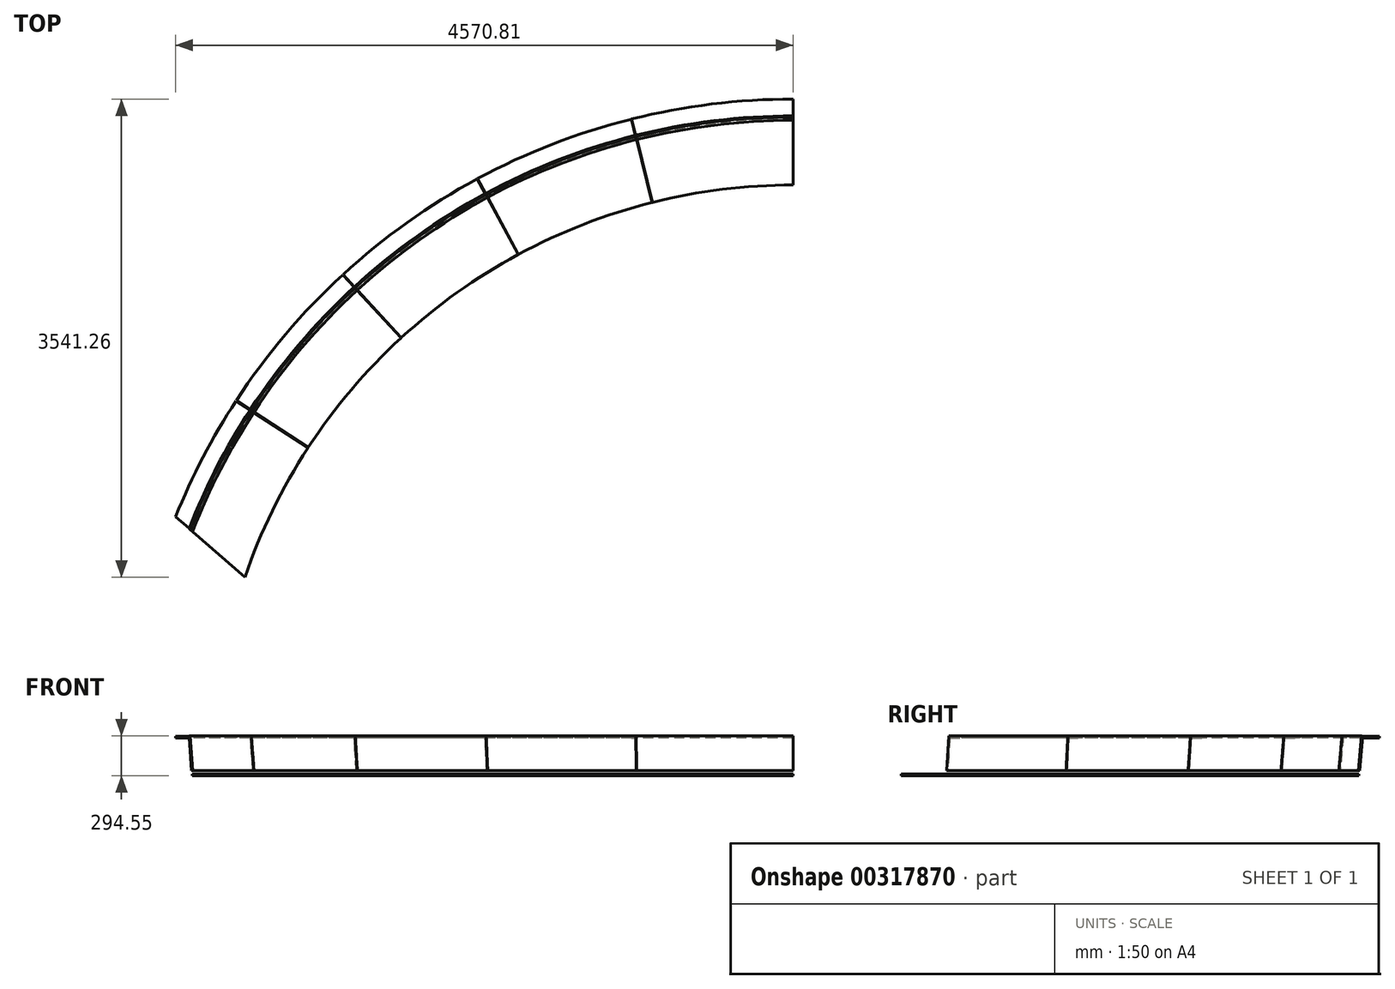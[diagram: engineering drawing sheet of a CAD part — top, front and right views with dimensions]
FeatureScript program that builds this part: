
annotation { "Feature Type Name" : "Feature", "Feature Type Description" : "" }
export const myFeature = defineFeature(function(context is Context, id is Id, definition is map)
    precondition{}
    {
        {
            var Q0;
            Q0=qCreatedBy(makeId("Top.planeOp"),FACE);
            var sketch = newSketch(context, id + "F0", { "sketchPlane" : qUnion([Q0])});
            skLineSegment(sketch, "E0", {"start": v(0, 0) * mm, "end": v(0, 473.08) * mm});
            skArc(sketch, "E1", {"start": v(0, 0) * mm, "mid": v(-2501.9, -802.3) * mm, "end": v(-4070.65, -2909.96) * mm});
            skLineSegment(sketch, "E2", {"start": v(-4070.65, -2909.96) * mm, "end": v(-4575.56, -2468.8) * mm});
            skLineSegment(sketch, "E3", {"start": v(0, 473.08) * mm, "end": v(0, 627.06) * mm});
            skArc(sketch, "E4", {"start": v(0, 627.06) * mm, "mid": v(-2762.25, -219.62) * mm, "end": v(-4575.56, -2468.8) * mm});
            skArc(sketch, "E5", {"start": v(0, 473.07) * mm, "mid": v(-2698.3, -362.37) * mm, "end": v(-4452.45, -2576.36) * mm});
            skArc(sketch, "E6", {"start": v(0, 498.48) * mm, "mid": v(-2708.85, -338.8) * mm, "end": v(-4472.79, -2558.6) * mm});
            skLineSegment(sketch, "E7", {"start": v(-1198.89, 479.04) * mm, "end": v(-1046.37, -129.2) * mm});
            skLineSegment(sketch, "E8", {"start": v(-2042.06, -515.53) * mm, "end": v(-2339.7, 36.39) * mm});
            skLineSegment(sketch, "E9", {"start": v(-2911.9, -1135.24) * mm, "end": v(-3336.32, -673.65) * mm});
            skLineSegment(sketch, "E10", {"start": v(-3602.27, -1950.12) * mm, "end": v(-4127.33, -1607.3) * mm});
            skSolve(sketch);
        }
        {
            var Q0;
            Q0=qCreatedBy(makeId("Top.planeOp"),FACE);
            var sketch = newSketch(context, id + "F1", { "sketchPlane" : qUnion([Q0])});
            skArc(sketch, "E11.0", {"start": v(-1.59, -12.7) * mm, "mid": v(-2497.27, -814.6) * mm, "end": v(-4060.3, -2919) * mm});
            skLineSegment(sketch, "E12.0", {"start": v(-4059.75, -2917.37) * mm, "end": v(-4449.3, -2577.01) * mm});
            skArc(sketch, "E13.0", {"start": v(-1.59, 469.9) * mm, "mid": v(-2696.94, -365.28) * mm, "end": v(-4449.3, -2577.01) * mm});
            skLineSegment(sketch, "E14.0", {"start": v(-1.59, -12.7) * mm, "end": v(-1.59, 469.9) * mm});
            skLineSegment(sketch, "E15.0", {"start": v(-1162.2, 326.21) * mm, "end": v(-1044.82, -141.9) * mm});
            skLineSegment(sketch, "E16.0", {"start": v(-1159.12, 326.98) * mm, "end": v(-1041.74, -141.12) * mm});
            skLineSegment(sketch, "E17.0", {"start": v(-2034.63, -525.96) * mm, "end": v(-2263.7, -101.19) * mm});
            skLineSegment(sketch, "E18.0", {"start": v(-2037.43, -527.47) * mm, "end": v(-2266.5, -102.7) * mm});
            skLineSegment(sketch, "E19.0", {"start": v(-2902.13, -1143.52) * mm, "end": v(-3228.78, -788.27) * mm});
            skLineSegment(sketch, "E20.0", {"start": v(-2904.47, -1145.67) * mm, "end": v(-3231.12, -790.41) * mm});
            skLineSegment(sketch, "E21.0", {"start": v(-3592.5, -1958.4) * mm, "end": v(-3996.6, -1694.56) * mm});
            skLineSegment(sketch, "E22.0", {"start": v(-3590.77, -1955.74) * mm, "end": v(-3994.86, -1691.9) * mm});
            skSolve(sketch);
        }
        {
            var Q0;
            {var subQ0=sQuery(id+"F1.wireOp",EDGE,"E12.0");Q0=makeQuery(id+"F1.imprint","IMPRINT",FACE,{"disambiguationData":[TD([[makeQuery(id+"F1.imprint","IMPRINT",EDGE,{"derivedFrom":subQ0}),-1.0]])]});}
            var Q1;
            {var subQ0=sQuery(id+"F1.wireOp",EDGE,"E20.0");Q1=makeQuery(id+"F1.imprint","IMPRINT",FACE,{"disambiguationData":[TD([[makeQuery(id+"F1.imprint","IMPRINT",EDGE,{"derivedFrom":subQ0}),1.0]])]});}
            var Q2;
            {var subQ0=sQuery(id+"F1.wireOp",EDGE,"E18.0");Q2=makeQuery(id+"F1.imprint","IMPRINT",FACE,{"disambiguationData":[TD([[makeQuery(id+"F1.imprint","IMPRINT",EDGE,{"derivedFrom":subQ0}),1.0]])]});}
            var Q3;
            {var subQ0=sQuery(id+"F1.wireOp",EDGE,"E15.0");Q3=makeQuery(id+"F1.imprint","IMPRINT",FACE,{"disambiguationData":[TD([[makeQuery(id+"F1.imprint","IMPRINT",EDGE,{"derivedFrom":subQ0}),-1.0]])]});}
            var Q4;
            {var subQ0=sQuery(id+"F1.wireOp",EDGE,"E14.0");Q4=makeQuery(id+"F1.imprint","IMPRINT",FACE,{"disambiguationData":[TD([[makeQuery(id+"F1.imprint","IMPRINT",EDGE,{"derivedFrom":subQ0}),1.0]])]});}
            extrude(context, id + "F2", {"entities" : qUnion([Q0, Q1, Q2, Q3, Q4]), "depth" : 12.7 * mm});
        }
        {
            var Q0;
            Q0=qCreatedBy(makeId("Top.planeOp"),FACE);
            cPlane(context, id + "F3", {"entities" : qUnion([Q0]), "cplaneType" : CPlaneType.OFFSET, "offset" : 281 * mm, "width" : 152.4 * mm, "height" : 152.4 * mm});
        }
        {
            var Q0;
            Q0=qCreatedBy(id+"F3.planeOp",FACE);
            var sketch = newSketch(context, id + "F4", { "sketchPlane" : qUnion([Q0])});
            skLineSegment(sketch, "E23.0", {"start": v(-1196.58, 476.35) * mm, "end": v(-1166.07, 354.7) * mm});
            skLineSegment(sketch, "E24.0", {"start": v(-1199.66, 475.58) * mm, "end": v(-1169.15, 353.93) * mm});
            skLineSegment(sketch, "E25.0", {"start": v(-2277.27, -76.04) * mm, "end": v(-2336.8, 34.35) * mm});
            skLineSegment(sketch, "E26.0", {"start": v(-2280.06, -77.55) * mm, "end": v(-2339.6, 32.84) * mm});
            skLineSegment(sketch, "E27.0", {"start": v(-3248.12, -767.23) * mm, "end": v(-3333, -674.91) * mm});
            skLineSegment(sketch, "E28.0", {"start": v(-3250.46, -769.38) * mm, "end": v(-3335.34, -677.06) * mm});
            skLineSegment(sketch, "E29.0", {"start": v(-4018.8, -1676.28) * mm, "end": v(-4123.8, -1607.71) * mm});
            skLineSegment(sketch, "E30.0", {"start": v(-4020.53, -1678.93) * mm, "end": v(-4125.54, -1610.37) * mm});
            skLineSegment(sketch, "E31.0", {"start": v(-4472.18, -2557.02) * mm, "end": v(-4572.4, -2469.44) * mm});
            skLineSegment(sketch, "E32.0", {"start": v(-1.59, 498.47) * mm, "end": v(-1.59, 623.89) * mm});
            skArc(sketch, "E33.0", {"start": v(-1.59, 623.89) * mm, "mid": v(-2761.13, -222.7) * mm, "end": v(-4572.62, -2469.97) * mm});
            skArc(sketch, "E34.0", {"start": v(-1.59, 498.47) * mm, "mid": v(-2708.8, -338.78) * mm, "end": v(-4472.18, -2557.02) * mm});
            skPoint(sketch, "E35.orphan", {"position": v(-4449.3, -2577.01) * mm});
            skPoint(sketch, "E36.orphan", {"position": v(-3996.6, -1694.56) * mm});
            skPoint(sketch, "E37.orphan", {"position": v(-3994.86, -1691.9) * mm});
            skPoint(sketch, "E38.orphan", {"position": v(-3231.12, -790.41) * mm});
            skPoint(sketch, "E39.orphan", {"position": v(-3228.78, -788.27) * mm});
            skPoint(sketch, "E40.orphan", {"position": v(-2263.7, -101.19) * mm});
            skPoint(sketch, "E41.orphan", {"position": v(-2266.5, -102.7) * mm});
            skPoint(sketch, "E42.orphan", {"position": v(-1159.12, 326.98) * mm});
            skPoint(sketch, "E43.orphan", {"position": v(-1162.2, 326.21) * mm});
            skPoint(sketch, "E44.orphan", {"position": v(-1.59, 469.9) * mm});
            skPoint(sketch, "E45.orphan", {"position": v(-4059.75, -2917.37) * mm});
            skPoint(sketch, "E46.orphan", {"position": v(-3590.77, -1955.74) * mm});
            skPoint(sketch, "E47.orphan", {"position": v(-2904.47, -1145.67) * mm});
            skPoint(sketch, "E48.orphan", {"position": v(-2037.43, -527.47) * mm});
            skPoint(sketch, "E49.orphan", {"position": v(-2902.13, -1143.52) * mm});
            skPoint(sketch, "E50.orphan", {"position": v(-3592.5, -1958.4) * mm});
            skPoint(sketch, "E51.orphan", {"position": v(-2034.63, -525.96) * mm});
            skPoint(sketch, "E52.orphan", {"position": v(-1041.74, -141.12) * mm});
            skPoint(sketch, "E53.orphan", {"position": v(-1044.82, -141.9) * mm});
            skPoint(sketch, "E54.orphan", {"position": v(-1.59, -12.7) * mm});
            skPoint(sketch, "E55.orphan", {"position": v(0, 498.48) * mm});
            skPoint(sketch, "E56.orphan", {"position": v(-4472.79, -2558.6) * mm});
            skSolve(sketch);
        }
        {
            var Q0;
            {var subQ0=sQuery(id+"F4.wireOp",EDGE,"E30.0");Q0=makeQuery(id+"F4.imprint","IMPRINT",FACE,{"disambiguationData":[TD([[makeQuery(id+"F4.imprint","IMPRINT",EDGE,{"derivedFrom":subQ0}),1.0]])]});}
            var Q1;
            {var subQ0=sQuery(id+"F4.wireOp",EDGE,"E28.0");Q1=makeQuery(id+"F4.imprint","IMPRINT",FACE,{"disambiguationData":[TD([[makeQuery(id+"F4.imprint","IMPRINT",EDGE,{"derivedFrom":subQ0}),1.0]])]});}
            var Q2;
            {var subQ0=sQuery(id+"F4.wireOp",EDGE,"E26.0");Q2=makeQuery(id+"F4.imprint","IMPRINT",FACE,{"disambiguationData":[TD([[makeQuery(id+"F4.imprint","IMPRINT",EDGE,{"derivedFrom":subQ0}),1.0]])]});}
            var Q3;
            {var subQ0=sQuery(id+"F4.wireOp",EDGE,"E24.0");Q3=makeQuery(id+"F4.imprint","IMPRINT",FACE,{"disambiguationData":[TD([[makeQuery(id+"F4.imprint","IMPRINT",EDGE,{"derivedFrom":subQ0}),-1.0]])]});}
            var Q4;
            {var subQ0=sQuery(id+"F4.wireOp",EDGE,"E23.0");Q4=makeQuery(id+"F4.imprint","IMPRINT",FACE,{"disambiguationData":[TD([[makeQuery(id+"F4.imprint","IMPRINT",EDGE,{"derivedFrom":subQ0}),1.0]])]});}
            extrude(context, id + "F5", {"entities" : qUnion([Q0, Q1, Q2, Q3, Q4]), "depth" : 12.7 * mm});
        }
        {
            var Q0;
            Q0=makeQuery(id+"F5.opExtrude","SWEPT_FACE",FACE,{"disambiguationData":[OSD([sQuery(id+"F4.wireOp",EDGE,"E32.0")])]});
            var sketch = newSketch(context, id + "F6", { "sketchPlane" : qUnion([Q0])});
            skLineSegment(sketch, "E57", {"start": v(499.62, 293.69) * mm, "end": v(476.44, 37.24) * mm});
            skLineSegment(sketch, "E58", {"start": v(476.44, 37.24) * mm, "end": v(466.96, 38.1) * mm});
            skLineSegment(sketch, "E59", {"start": v(466.96, 38.1) * mm, "end": v(490.14, 294.55) * mm});
            skLineSegment(sketch, "E60", {"start": v(490.14, 294.55) * mm, "end": v(499.62, 293.69) * mm});
            skSolve(sketch);
        }
        {
            var Q0;
            {var subQ1=sQuery(id+"F6.wireOp",EDGE,"E58");Q0=makeQuery(id+"F6.imprint","IMPRINT",FACE,{"disambiguationData":[TD([[makeQuery(id+"F6.imprint","IMPRINT",EDGE,{"derivedFrom":subQ1}),-1.0]])]});}
            var Q1;
            {var subQ1=sQuery(id+"F4.wireOp",EDGE,"E32.0");var subQ6=makeQuery(id+"F5.opExtrude","SWEPT_EDGE",EDGE,{"disambiguationData":[OSD([subQ1,sQuery(id+"F4.wireOp",EDGE,"E34.0")])]});Q1=makeQuery(id+"F6.imprint","IMPRINT",FACE,{"disambiguationData":[TD([[makeQuery(id+"F6.imprint","IMPRINT",EDGE,{"derivedFrom":subQ6}),1.0]])]});}
            var Q2;
            Q2=sQuery(id+"F4.wireOp",EDGE,"E34.0");
            sweep(context, id + "F7", {"profiles" : qUnion([Q0, Q1]), "path" : qUnion([Q2])});
        }
        {
            var Q0;
            Q0=makeQuery(id+"F7.opSweep","CAP_FACE",FACE,{"disambiguationData":[OSD([sQuery(id+"F4.wireOp",VERTEX,"E34.0.end"),sQuery(id+"F6.wireOp",EDGE,"E57"),sQuery(id+"F6.wireOp",EDGE,"E58"),sQuery(id+"F6.wireOp",EDGE,"E59"),sQuery(id+"F6.wireOp",EDGE,"E60")])],"isStart":false});
            var Q1;
            Q1=makeQuery(id+"F2.opExtrude","SWEPT_FACE",FACE,{"disambiguationData":[OSD([sQuery(id+"F1.wireOp",EDGE,"E12.0")])]});
            extrude(context, id + "F8", {"entities" : qUnion([Q0]), "operationType" : NewBodyOperationType.ADD, "endBound" : BoundingType.UP_TO_SURFACE, "endBoundEntityFace" : qUnion([Q1]), "depth" : 25.4 * mm});
        }
        {
            var Q0;
            Q0=qCreatedBy(makeId("Top.planeOp"),FACE);
            var sketch = newSketch(context, id + "F9", { "sketchPlane" : qUnion([Q0])});
            skLineSegment(sketch, "E61.0", {"start": v(-3603.14, -1951.45) * mm, "end": v(-4128.2, -1608.63) * mm});
            skLineSegment(sketch, "E62.0", {"start": v(-3601.4, -1948.8) * mm, "end": v(-4126.46, -1605.98) * mm});
            skPoint(sketch, "E63.orphan", {"position": v(-4020.53, -1678.93) * mm});
            skPoint(sketch, "E64.orphan", {"position": v(-4018.8, -1676.28) * mm});
            skArc(sketch, "E65.0", {"start": v(0, 627.06) * mm, "mid": v(-2762.25, -219.62) * mm, "end": v(-4575.56, -2468.8) * mm});
            skArc(sketch, "E66.0", {"start": v(0, 0) * mm, "mid": v(-2501.9, -802.3) * mm, "end": v(-4070.65, -2909.96) * mm});
            skLineSegment(sketch, "E67.0", {"start": v(-2913.06, -1136.32) * mm, "end": v(-3337.5, -674.72) * mm});
            skLineSegment(sketch, "E68.0", {"start": v(-2910.73, -1134.17) * mm, "end": v(-3335.15, -672.57) * mm});
            skPoint(sketch, "E69.orphan", {"position": v(-3248.12, -767.23) * mm});
            skPoint(sketch, "E70.orphan", {"position": v(-3250.46, -769.38) * mm});
            skPoint(sketch, "E71.orphan", {"position": v(-3335.34, -677.06) * mm});
            skPoint(sketch, "E72.orphan", {"position": v(-3333, -674.91) * mm});
            skPoint(sketch, "E73.orphan", {"position": v(-4125.54, -1610.37) * mm});
            skPoint(sketch, "E74.orphan", {"position": v(-4123.8, -1607.71) * mm});
            skLineSegment(sketch, "E75.0", {"start": v(-2043.46, -516.29) * mm, "end": v(-2341.1, 35.63) * mm});
            skLineSegment(sketch, "E76.0", {"start": v(-2040.66, -514.78) * mm, "end": v(-2338.3, 37.14) * mm});
            skPoint(sketch, "E77.orphan", {"position": v(-2266.5, -102.7) * mm});
            skPoint(sketch, "E78.orphan", {"position": v(-2263.7, -101.19) * mm});
            skPoint(sketch, "E79.orphan", {"position": v(-2037.43, -527.47) * mm});
            skPoint(sketch, "E80.orphan", {"position": v(-2034.63, -525.96) * mm});
            skLineSegment(sketch, "E81.0", {"start": v(-1197.35, 479.43) * mm, "end": v(-1044.83, -128.8) * mm});
            skLineSegment(sketch, "E82.0", {"start": v(-1200.43, 478.66) * mm, "end": v(-1047.91, -129.58) * mm});
            skPoint(sketch, "E83.orphan", {"position": v(-1044.82, -141.9) * mm});
            skPoint(sketch, "E84.orphan", {"position": v(-1041.74, -141.12) * mm});
            skPoint(sketch, "E85.orphan", {"position": v(-1162.2, 326.21) * mm});
            skPoint(sketch, "E86.orphan", {"position": v(-1159.12, 326.98) * mm});
            skLineSegment(sketch, "E87.0", {"start": v(0, 0) * mm, "end": v(0, 627.06) * mm});
            skLineSegment(sketch, "E88.0", {"start": v(-1.59, 0) * mm, "end": v(-1.59, 627.06) * mm});
            skPoint(sketch, "E89.orphan", {"position": v(-1.59, 469.9) * mm});
            skPoint(sketch, "E90.orphan", {"position": v(0, 473.08) * mm});
            skPoint(sketch, "E91.orphan", {"position": v(-1.59, -12.7) * mm});
            skLineSegment(sketch, "E92.0", {"start": v(-4070.65, -2909.96) * mm, "end": v(-4575.56, -2468.8) * mm});
            skLineSegment(sketch, "E93.0", {"start": v(-4059.75, -2917.37) * mm, "end": v(-4574.94, -2467.23) * mm});
            skPoint(sketch, "E94.orphan", {"position": v(-4449.3, -2577.01) * mm});
            skSolve(sketch);
        }
        {
            var Q0;
            {var subQ0=sQuery(id+"F9.wireOp",EDGE,"E92.0");Q0=makeQuery(id+"F9.imprint","IMPRINT",FACE,{"disambiguationData":[TD([[makeQuery(id+"F9.imprint","IMPRINT",EDGE,{"derivedFrom":subQ0}),-1.0]])]});}
            var Q1;
            {var subQ0=sQuery(id+"F9.wireOp",EDGE,"E61.0");Q1=makeQuery(id+"F9.imprint","IMPRINT",FACE,{"disambiguationData":[TD([[makeQuery(id+"F9.imprint","IMPRINT",EDGE,{"derivedFrom":subQ0}),-1.0]])]});}
            var Q2;
            {var subQ0=sQuery(id+"F9.wireOp",EDGE,"E67.0");Q2=makeQuery(id+"F9.imprint","IMPRINT",FACE,{"disambiguationData":[TD([[makeQuery(id+"F9.imprint","IMPRINT",EDGE,{"derivedFrom":subQ0}),-1.0]])]});}
            var Q3;
            {var subQ0=sQuery(id+"F9.wireOp",EDGE,"E75.0");Q3=makeQuery(id+"F9.imprint","IMPRINT",FACE,{"disambiguationData":[TD([[makeQuery(id+"F9.imprint","IMPRINT",EDGE,{"derivedFrom":subQ0}),-1.0]])]});}
            var Q4;
            {var subQ0=sQuery(id+"F9.wireOp",EDGE,"E81.0");Q4=makeQuery(id+"F9.imprint","IMPRINT",FACE,{"disambiguationData":[TD([[makeQuery(id+"F9.imprint","IMPRINT",EDGE,{"derivedFrom":subQ0}),-1.0]])]});}
            var Q5;
            {var subQ0=sQuery(id+"F9.wireOp",EDGE,"E87.0");Q5=makeQuery(id+"F9.imprint","IMPRINT",FACE,{"disambiguationData":[TD([[makeQuery(id+"F9.imprint","IMPRINT",EDGE,{"derivedFrom":subQ0}),1.0]])]});}
            extrude(context, id + "F10", {"entities" : qUnion([Q0, Q1, Q2, Q3, Q4, Q5]), "operationType" : NewBodyOperationType.REMOVE, "endBound" : BoundingType.THROUGH_ALL, "depth" : 25.4 * mm});
        }
    });
